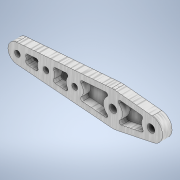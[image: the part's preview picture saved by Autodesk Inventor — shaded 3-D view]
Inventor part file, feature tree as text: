
AUTODESK INVENTOR PART (.ipt)
format: ipt  version: 2020.2 (Build 242310000, 310)  size: 286,208 bytes
history: native  units: mm
features: other x4, sketch x4, extrude x3, hole x2, fillet x2
ambient origin geometry x8: Origin, YZ Plane, XZ Plane, XY Plane, X Axis, Y Axis, Z Axis, Center Point
bodies: Body1 (feature_tree)
feature tree (15):
  other  "ソリッド1"
  sketch  "スケッチ1"
  extrude  "押し出し1"  Depth=130.0mm
  hole  "穴1"  [1 undecoded]
  extrude  "押し出し2"  Depth=35.0mm
  fillet  "フィレット1"  Radius=15.0mm
  extrude  "押し出し3"  Depth=10.0mm
  fillet  "フィレット2"  Radius=15.0mm
  hole  "穴2"  [1 undecoded]
  sketch  "スケッチ2"
  sketch  "スケッチ3"
  sketch  "スケッチ4"
  other  "断面エッジを投影1"
  other  "断面エッジを投影2"
  other  "断面エッジを投影3"
note: 2 required parameter values undecoded (feature->parameter linkage not recoverable at this tier; creation-order binding heuristic only, values carry confidence <= 0.55)
